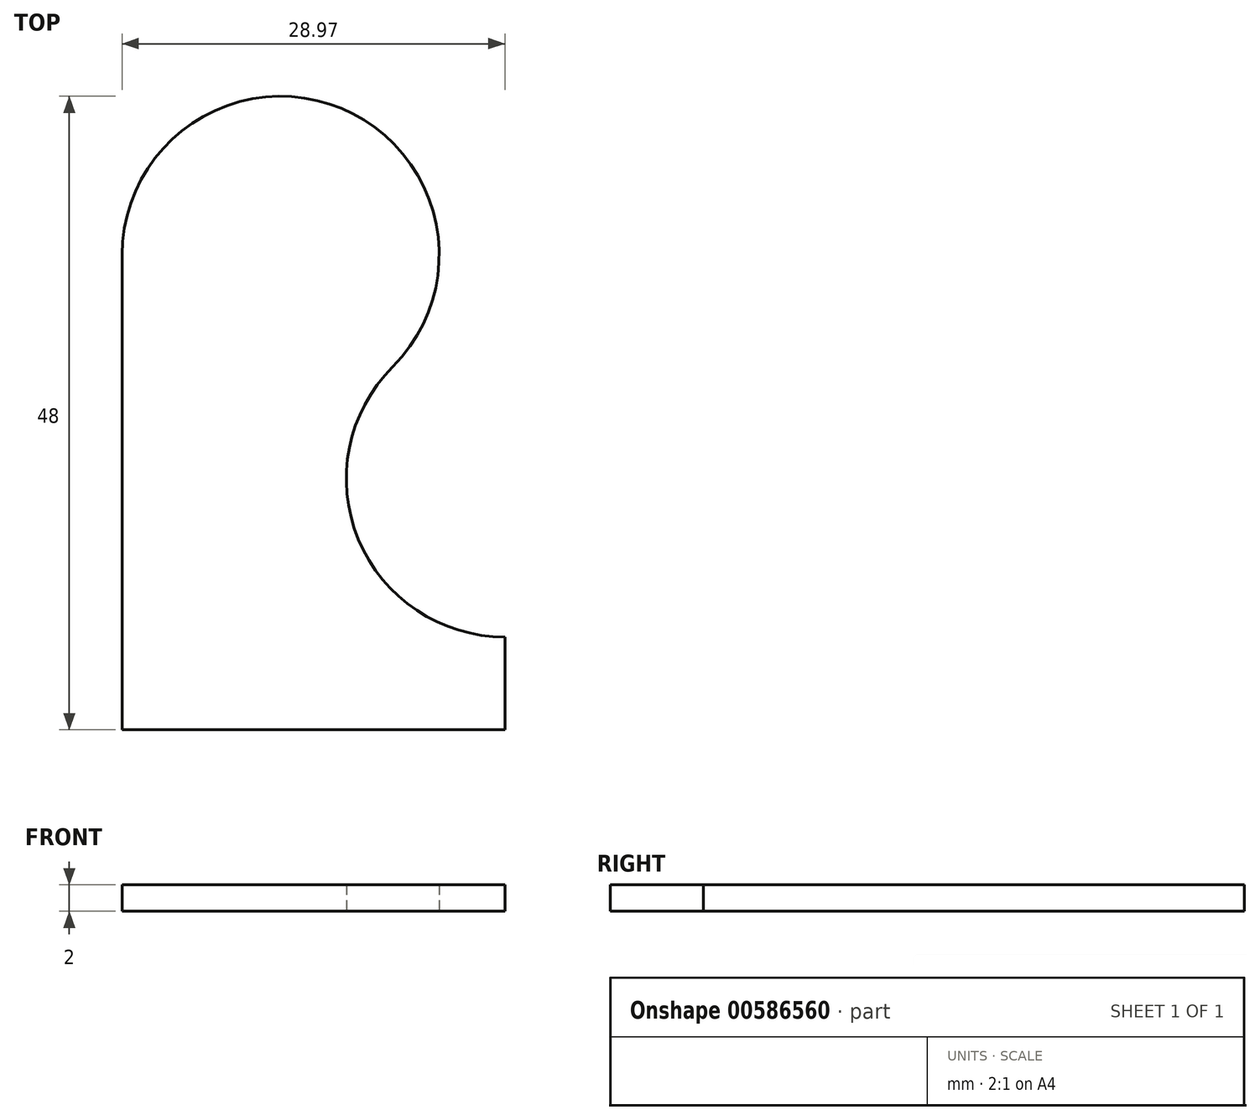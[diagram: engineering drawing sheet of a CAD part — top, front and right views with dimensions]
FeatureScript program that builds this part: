
annotation { "Feature Type Name" : "Feature", "Feature Type Description" : "" }
export const myFeature = defineFeature(function(context is Context, id is Id, definition is map)
    precondition{}
    {
        {
            var Q0;
            Q0=qCreatedBy(makeId("Top.planeOp"),FACE);
            var sketch = newSketch(context, id + "F0", { "sketchPlane" : qUnion([Q0])});
            skLineSegment(sketch, "E0", {"start": v(0, 0) * mm, "end": v(0, 36) * mm});
            skArc(sketch, "E1", {"start": v(0, 36) * mm, "mid": v(16.6, 47.09) * mm, "end": v(20.49, 27.51) * mm});
            skArc(sketch, "E2", {"start": v(20.49, 27.51) * mm, "mid": v(17.88, 14.44) * mm, "end": v(28.97, 7.03) * mm});
            skLineSegment(sketch, "E3", {"start": v(12, 36) * mm, "end": v(28.97, 19.03) * mm, "construction": true});
            skLineSegment(sketch, "E4", {"start": v(28.97, 0) * mm, "end": v(28.97, 19.03) * mm, "construction": true});
            skLineSegment(sketch, "E5", {"start": v(0, 0) * mm, "end": v(28.97, 0) * mm});
            skLineSegment(sketch, "E6", {"start": v(28.97, 7.03) * mm, "end": v(28.97, 0) * mm});
            skLineSegment(sketch, "E7", {"start": v(0, 36) * mm, "end": v(12, 36) * mm, "construction": true});
            skLineSegment(sketch, "E8", {"start": v(12, 36) * mm, "end": v(12, 24) * mm, "construction": true});
            skLineSegment(sketch, "E9", {"start": v(12, 24) * mm, "end": v(12, 12) * mm, "construction": true});
            skLineSegment(sketch, "E10", {"start": v(12, 0) * mm, "end": v(12, 12) * mm, "construction": true});
            skSolve(sketch);
        }
        {
            var Q0;
            Q0=qSketchRegion(id+"F0",true);
            extrude(context, id + "F1", {"entities" : qUnion([Q0]), "depth" : 2 * mm, "offsetDistance" : 25 * mm});
        }
    });
